# Revit family: Ottoman-Soft_Seating-Allermuir-Jaks-JA1
name_source: partatom
category: Furniture
revit_build: Autodesk Revit MEP 2012 (Build: 20110309_2315)
units: mm (PartAtom-declared; Revit-internal decimal feet)

## types (1)
- JA1
    04 CSI = 12 51 00
    95 CSI = 12510
    Assembly Code = E2020200
    Bench = Fabric - Allermuir - Silcoates
    Brochure URL = http://www.allermuir.net
    CAD Blocks URL = http://www.allermuir.net
    Color Availability = See price list for material options
    Fabric Spec Sheets = http://www.allermuir.net
    LEED Stats URL = http://www.allermuir.net
    Leg Base = Plastic - Allermuir - Black
    Legs = Metal - Allermuir - Chrome - Polished
    Manufacturer = Allermuir
    Manufacturer Fax = (419) 887 5805
    Model = JA1
    Overall Depth = 53 1/8"
    Overall Height = 19"
    Overall Width = 53 13/128"
    Plugin Data URL = http://products.ecoscorecard.com
    Pricing URL = http://www.allermuir.net
    Product Line = Jaks
    Product Page URL = http://www.allermuir.net
    Specifications URL = http://www.allermuir.net
    Subcategory = Soft Seating
    Thickness = 2 63/64"
    URL = http://www.allermuir.net
    Weight = 0.0 lb
    White Plastic Back Membrane = No
    ecoScorecard Product Page = http://products.ecoscorecard.com
    ecoScorecard_data = http://thesenatorgroup.ecoscorecard.com

## geometry (parser evidence)
native form markers: Blend x14, Sweep x2
no freeform markers — native parametric forms only
